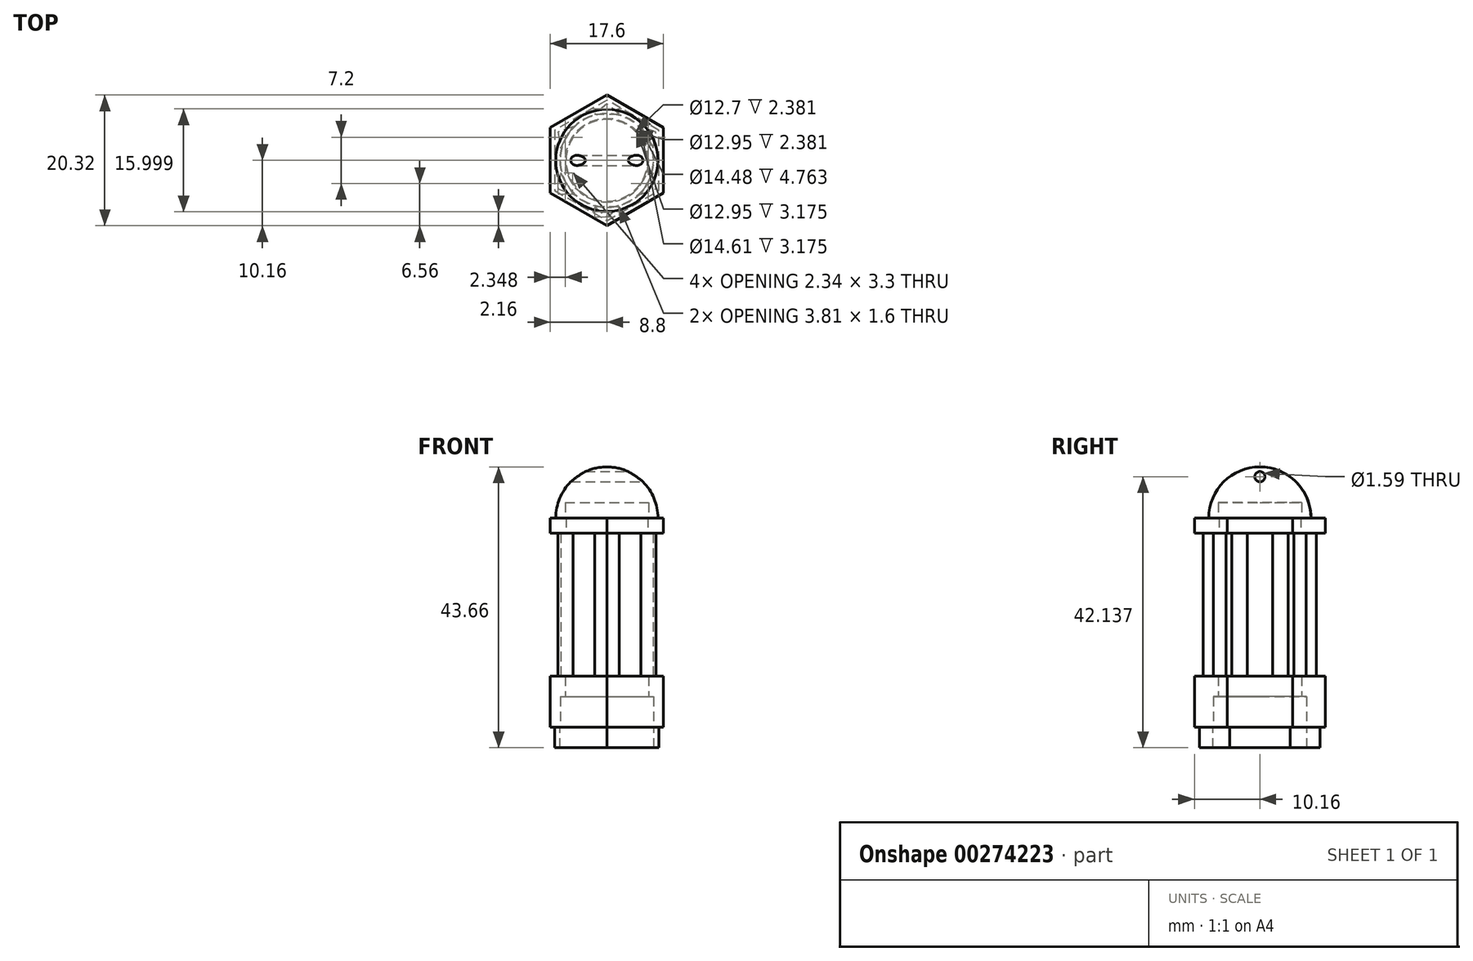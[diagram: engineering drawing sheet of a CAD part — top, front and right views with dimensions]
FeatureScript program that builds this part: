
annotation { "Feature Type Name" : "Feature", "Feature Type Description" : "" }
export const myFeature = defineFeature(function(context is Context, id is Id, definition is map)
    precondition{}
    {
        {
            var Q0;
            Q0=qCreatedBy(makeId("Top.planeOp"),FACE);
            var sketch = newSketch(context, id + "F0", { "sketchPlane" : qUnion([Q0])});
            skCircle(sketch, "E0.cCircle", {"center": v(0, 0) * mm, "radius": 10.16 * mm, "construction": true});
            skLineSegment(sketch, "E0.0", {"start": v(0, 10.16) * mm, "end": v(8.8, 5.08) * mm});
            skLineSegment(sketch, "E0.1", {"start": v(8.8, 5.08) * mm, "end": v(8.8, -5.08) * mm});
            skLineSegment(sketch, "E0.2", {"start": v(8.8, -5.08) * mm, "end": v(0, -10.16) * mm});
            skLineSegment(sketch, "E0.3", {"start": v(0, -10.16) * mm, "end": v(-8.8, -5.08) * mm});
            skLineSegment(sketch, "E0.4", {"start": v(-8.8, -5.08) * mm, "end": v(-8.8, 5.08) * mm});
            skLineSegment(sketch, "E0.5", {"start": v(-8.8, 5.08) * mm, "end": v(0, 10.16) * mm});
            skSolve(sketch);
        }
        {
            var Q0;
            Q0 = qSketchRegion(id + "F0", true);
            extrude(context, id + "F1", {"entities" : qUnion([Q0]), "depth" : 7.94 * mm});
        }
        {
            var Q0;
            Q0=makeQuery(id+"F1.opExtrude","CAP_FACE",FACE,{"disambiguationData":[OSD([sQuery(id+"F0.wireOp",EDGE,"E0.0"),sQuery(id+"F0.wireOp",EDGE,"E0.1"),sQuery(id+"F0.wireOp",EDGE,"E0.2"),sQuery(id+"F0.wireOp",EDGE,"E0.3"),sQuery(id+"F0.wireOp",EDGE,"E0.4"),sQuery(id+"F0.wireOp",EDGE,"E0.5")])],"isStart":false});
            var sketch = newSketch(context, id + "F2", { "sketchPlane" : qUnion([Q0])});
            skCircle(sketch, "E1", {"center": v(0, 0) * mm, "radius": 8.8 * mm, "construction": true});
            skCircle(sketch, "E2", {"center": v(0, 0) * mm, "radius": 7.2 * mm, "construction": true});
            skLineSegment(sketch, "E3", {"start": v(0, 8.8) * mm, "end": v(-1.9, 7.2) * mm});
            skLineSegment(sketch, "E4", {"start": v(-1.9, 7.2) * mm, "end": v(1.9, 7.2) * mm});
            skLineSegment(sketch, "E5", {"start": v(1.9, 7.2) * mm, "end": v(0, 8.8) * mm});
            skLineSegment(sketch, "E6.1.0", {"start": v(-7.62, 4.4) * mm, "end": v(-7.19, 1.95) * mm});
            skLineSegment(sketch, "E6.1.1", {"start": v(-5.28, 5.25) * mm, "end": v(-7.62, 4.4) * mm});
            skLineSegment(sketch, "E6.1.2", {"start": v(-7.19, 1.95) * mm, "end": v(-5.28, 5.25) * mm});
            skLineSegment(sketch, "E6.2.0", {"start": v(-7.62, -4.4) * mm, "end": v(-5.28, -5.25) * mm});
            skLineSegment(sketch, "E6.2.1", {"start": v(-7.19, -1.95) * mm, "end": v(-7.62, -4.4) * mm});
            skLineSegment(sketch, "E6.2.2", {"start": v(-5.28, -5.25) * mm, "end": v(-7.19, -1.95) * mm});
            skLineSegment(sketch, "E6.3.0", {"start": v(0, -8.8) * mm, "end": v(1.9, -7.2) * mm});
            skLineSegment(sketch, "E6.3.1", {"start": v(-1.9, -7.2) * mm, "end": v(0, -8.8) * mm});
            skLineSegment(sketch, "E6.3.2", {"start": v(1.9, -7.2) * mm, "end": v(-1.9, -7.2) * mm});
            skLineSegment(sketch, "E6.4.0", {"start": v(7.62, -4.4) * mm, "end": v(7.19, -1.95) * mm});
            skLineSegment(sketch, "E6.4.1", {"start": v(5.28, -5.25) * mm, "end": v(7.62, -4.4) * mm});
            skLineSegment(sketch, "E6.4.2", {"start": v(7.19, -1.95) * mm, "end": v(5.28, -5.25) * mm});
            skLineSegment(sketch, "E6.5.0", {"start": v(7.62, 4.4) * mm, "end": v(5.28, 5.25) * mm});
            skLineSegment(sketch, "E6.5.1", {"start": v(7.19, 1.95) * mm, "end": v(7.62, 4.4) * mm});
            skLineSegment(sketch, "E6.5.2", {"start": v(5.28, 5.25) * mm, "end": v(7.19, 1.95) * mm});
            skSolve(sketch);
        }
        {
            var Q0;
            Q0 = qSketchRegion(id + "F2", true);
            extrude(context, id + "F3", {"entities" : qUnion([Q0]), "operationType" : NewBodyOperationType.ADD, "depth" : 22.22 * mm});
        }
        {
            var Q0;
            Q0=makeQuery(id+"F3.opExtrude","CAP_FACE",FACE,{"disambiguationData":[OSD([sQuery(id+"F2.wireOp",EDGE,"E6.5.0"),sQuery(id+"F2.wireOp",EDGE,"E6.5.1"),sQuery(id+"F2.wireOp",EDGE,"E6.5.2")])],"isStart":false});
            var sketch = newSketch(context, id + "F4", { "sketchPlane" : qUnion([Q0])});
            skCircle(sketch, "E7.cCircle", {"center": v(0, 0) * mm, "radius": 10.16 * mm, "construction": true});
            skLineSegment(sketch, "E7.0", {"start": v(0, 10.16) * mm, "end": v(8.8, 5.08) * mm});
            skLineSegment(sketch, "E7.1", {"start": v(8.8, 5.08) * mm, "end": v(8.8, -5.08) * mm});
            skLineSegment(sketch, "E7.2", {"start": v(8.8, -5.08) * mm, "end": v(0, -10.16) * mm});
            skLineSegment(sketch, "E7.3", {"start": v(0, -10.16) * mm, "end": v(-8.8, -5.08) * mm});
            skLineSegment(sketch, "E7.4", {"start": v(-8.8, -5.08) * mm, "end": v(-8.8, 5.08) * mm});
            skLineSegment(sketch, "E7.5", {"start": v(-8.8, 5.08) * mm, "end": v(0, 10.16) * mm});
            skCircle(sketch, "E8", {"center": v(0, 0) * mm, "radius": 6.35 * mm});
            skSolve(sketch);
        }
        {
            var Q0;
            Q0 = qSketchRegion(id + "F4", true);
            extrude(context, id + "F5", {"entities" : qUnion([Q0]), "operationType" : NewBodyOperationType.ADD, "depth" : 2.38 * mm});
        }
        {
            var Q0;
            Q0=qCreatedBy(makeId("Right.planeOp"),FACE);
            var sketch = newSketch(context, id + "F6", { "sketchPlane" : qUnion([Q0])});
            skLineSegment(sketch, "E9", {"start": v(0, 34.93) * mm, "end": v(-6.48, 34.93) * mm});
            skLineSegment(sketch, "E10", {"start": v(-6.48, 34.93) * mm, "end": v(-6.48, 32.54) * mm});
            skArc(sketch, "E11", {"start": v(0, 40.48) * mm, "mid": v(-5.61, 38.16) * mm, "end": v(-7.94, 32.54) * mm});
            skLineSegment(sketch, "E12", {"start": v(0, 40.48) * mm, "end": v(0, 34.93) * mm});
            skLineSegment(sketch, "E13", {"start": v(-7.94, 32.54) * mm, "end": v(-6.48, 32.54) * mm});
            skLineSegment(sketch, "E14", {"start": v(0, 40.48) * mm, "end": v(0, 32.54) * mm, "construction": true});
            skLineSegment(sketch, "E15", {"start": v(0, 32.54) * mm, "end": v(-7.94, 32.54) * mm, "construction": true});
            skSolve(sketch);
        }
        {
            var Q0;
            Q0 = qSketchRegion(id + "F6", true);
            var Q1;
            Q1=makeQuery(id+"F5.opExtrude","CAP_EDGE",EDGE,{"disambiguationData":[OSD([sQuery(id+"F4.wireOp",EDGE,"E8")])],"isStart":false});
            revolve(context, id + "F7", {"operationType" : NewBodyOperationType.ADD, "entities" : qUnion([Q0]), "axis" : qUnion([Q1]), "revolveType" : RevolveType.FULL});
        }
        {
            var Q0;
            Q0=makeQuery(id+"F1.opExtrude","CAP_FACE",FACE,{"disambiguationData":[OSD([sQuery(id+"F0.wireOp",EDGE,"E0.0"),sQuery(id+"F0.wireOp",EDGE,"E0.1"),sQuery(id+"F0.wireOp",EDGE,"E0.2"),sQuery(id+"F0.wireOp",EDGE,"E0.3"),sQuery(id+"F0.wireOp",EDGE,"E0.4"),sQuery(id+"F0.wireOp",EDGE,"E0.5")])],"isStart":true});
            var sketch = newSketch(context, id + "F8", { "sketchPlane" : qUnion([Q0])});
            skCircle(sketch, "E16", {"center": v(0, 0) * mm, "radius": 7.24 * mm});
            skSolve(sketch);
        }
        {
            var Q0;
            Q0 = qSketchRegion(id + "F8", true);
            extrude(context, id + "F9", {"entities" : qUnion([Q0]), "operationType" : NewBodyOperationType.REMOVE, "oppositeDirection" : true, "depth" : 4.76 * mm});
        }
        {
            var Q0;
            Q0=makeQuery(id+"F9.boolean.opBoolean","COPY",FACE,{"derivedFrom":makeQuery(id+"F9.opExtrude","CAP_FACE",FACE,{"disambiguationData":[OSD([sQuery(id+"F8.wireOp",EDGE,"E16")])],"isStart":false})});
            var sketch = newSketch(context, id + "F10", { "sketchPlane" : qUnion([Q0])});
            skCircle(sketch, "E17", {"center": v(0, 0) * mm, "radius": 6.48 * mm});
            skSolve(sketch);
        }
        {
            var Q0;
            Q0 = qSketchRegion(id + "F10", true);
            extrude(context, id + "F11", {"entities" : qUnion([Q0]), "operationType" : NewBodyOperationType.REMOVE, "endBound" : BoundingType.UP_TO_NEXT, "oppositeDirection" : true, "depth" : 25.4 * mm});
        }
        {
            var Q0;
            Q0=makeQuery(id+"F1.opExtrude","CAP_FACE",FACE,{"disambiguationData":[OSD([sQuery(id+"F0.wireOp",EDGE,"E0.0"),sQuery(id+"F0.wireOp",EDGE,"E0.1"),sQuery(id+"F0.wireOp",EDGE,"E0.2"),sQuery(id+"F0.wireOp",EDGE,"E0.3"),sQuery(id+"F0.wireOp",EDGE,"E0.4"),sQuery(id+"F0.wireOp",EDGE,"E0.5")])],"isStart":true});
            var sketch = newSketch(context, id + "F12", { "sketchPlane" : qUnion([Q0])});
            skCircle(sketch, "E18", {"center": v(0, 0) * mm, "radius": 7.3 * mm});
            skCircle(sketch, "E19.cCircle", {"center": v(0, 0) * mm, "radius": 9.37 * mm, "construction": true});
            skLineSegment(sketch, "E19.0", {"start": v(0, -9.37) * mm, "end": v(-8.11, -4.68) * mm});
            skLineSegment(sketch, "E19.1", {"start": v(-8.11, -4.68) * mm, "end": v(-8.11, 4.68) * mm});
            skLineSegment(sketch, "E19.2", {"start": v(-8.11, 4.68) * mm, "end": v(0, 9.37) * mm});
            skLineSegment(sketch, "E19.3", {"start": v(0, 9.37) * mm, "end": v(8.11, 4.68) * mm});
            skLineSegment(sketch, "E19.4", {"start": v(8.11, 4.68) * mm, "end": v(8.11, -4.68) * mm});
            skLineSegment(sketch, "E19.5", {"start": v(8.11, -4.68) * mm, "end": v(0, -9.37) * mm});
            skSolve(sketch);
        }
        {
            var Q0;
            Q0 = qSketchRegion(id + "F12", true);
            extrude(context, id + "F13", {"entities" : qUnion([Q0]), "operationType" : NewBodyOperationType.ADD, "depth" : 3.17 * mm});
        }
        {
            var Q0;
            Q0=qCreatedBy(makeId("Right.planeOp"),FACE);
            var sketch = newSketch(context, id + "F14", { "sketchPlane" : qUnion([Q0])});
            skCircle(sketch, "E20", {"center": v(0, 38.96) * mm, "radius": 0.8 * mm});
            skLineSegment(sketch, "E21", {"start": v(-9.38, 40.48) * mm, "end": v(10.46, 40.48) * mm});
            skSolve(sketch);
        }
        {
            var Q0;
            Q0 = qSketchRegion(id + "F14", true);
            extrude(context, id + "F15", {"entities" : qUnion([Q0]), "operationType" : NewBodyOperationType.REMOVE, "endBound" : BoundingType.THROUGH_ALL, "oppositeDirection" : true, "depth" : 25.4 * mm, "hasSecondDirection" : true, "secondDirectionBound" : SecondDirectionBoundingType.THROUGH_ALL, "secondDirectionOppositeDirection" : false, "secondDirectionDepth" : 25.4 * mm});
        }
    });
